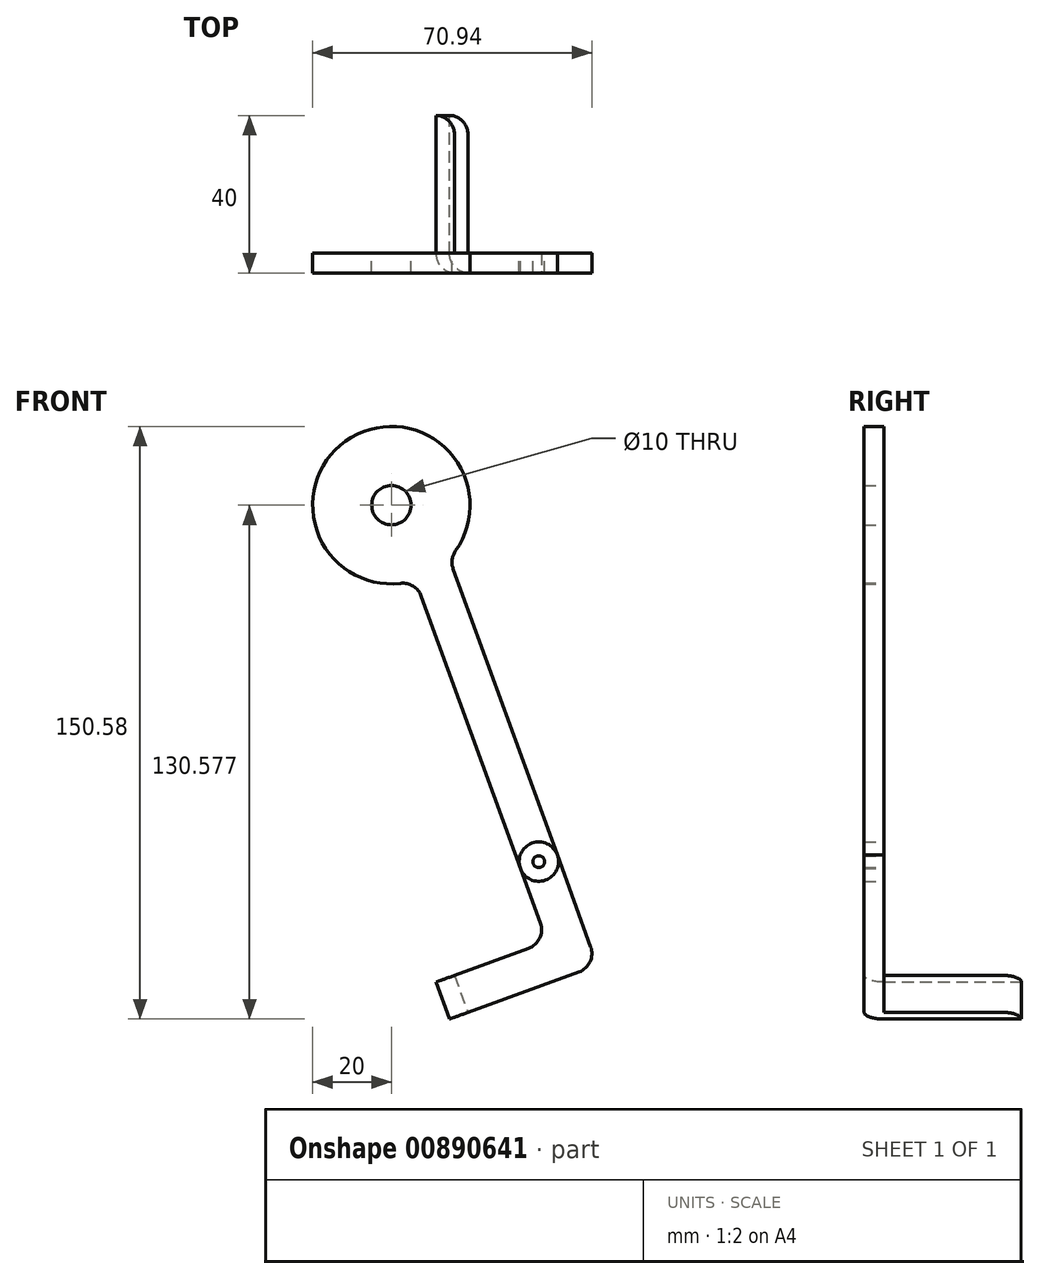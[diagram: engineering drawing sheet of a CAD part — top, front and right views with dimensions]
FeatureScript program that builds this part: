
annotation { "Feature Type Name" : "Feature", "Feature Type Description" : "" }
export const myFeature = defineFeature(function(context is Context, id is Id, definition is map)
    precondition{}
    {
        {
            var Q0;
            Q0=qCreatedBy(makeId("Front.planeOp"),FACE);
            var sketch = newSketch(context, id + "F0", { "sketchPlane" : qUnion([Q0])});
            skCircle(sketch, "E0", {"center": v(0, 33.82) * mm, "radius": 5 * mm});
            skLineSegment(sketch, "E1", {"start": v(0, 70.54) * mm, "end": v(0, -41.15) * mm, "construction": true});
            skCircle(sketch, "E2", {"center": v(0, 33.82) * mm, "radius": 20 * mm});
            skLineSegment(sketch, "E3.MirrorCS", {"start": v(36.77, -54.88) * mm, "end": v(32.07, -56.6) * mm, "construction": true});
            skLineSegment(sketch, "E4.MirrorCS", {"start": v(33.83, -60.2) * mm, "end": v(33.44, -60.35) * mm});
            skLineSegment(sketch, "E5.MirrorCS", {"start": v(32.46, -56.45) * mm, "end": v(32.07, -56.6) * mm});
            skLineSegment(sketch, "E6.MirrorCS", {"start": v(32.07, -56.6) * mm, "end": v(30.66, -57.1) * mm});
            skLineSegment(sketch, "E7.MirrorCS", {"start": v(30.66, -57.1) * mm, "end": v(32.03, -60.86) * mm});
            skLineSegment(sketch, "E8.MirrorCS", {"start": v(33.6, -60.82) * mm, "end": v(32.58, -58) * mm});
            skLineSegment(sketch, "E9.MirrorCS", {"start": v(37.45, -56.76) * mm, "end": v(38.14, -58.64) * mm, "construction": true});
            skLineSegment(sketch, "E10.MirrorCS", {"start": v(38.14, -58.64) * mm, "end": v(33.44, -60.35) * mm, "construction": true});
            skLineSegment(sketch, "E11.MirrorCS", {"start": v(37.45, -56.76) * mm, "end": v(36.77, -54.88) * mm, "construction": true});
            skCircle(sketch, "E12.MirrorC", {"center": v(37.45, -56.76) * mm, "radius": 1.5 * mm});
            skLineSegment(sketch, "E13.MirrorCS", {"start": v(30.66, -57.1) * mm, "end": v(25.92, -63.09) * mm});
            skLineSegment(sketch, "E14.MirrorCS", {"start": v(33.44, -60.35) * mm, "end": v(25.92, -63.09) * mm});
            skLineSegment(sketch, "E15.MirrorCS", {"start": v(24.55, -59.33) * mm, "end": v(25.92, -63.09) * mm});
            skLineSegment(sketch, "E16.MirrorCS", {"start": v(32.07, -56.6) * mm, "end": v(24.55, -59.33) * mm});
            skLineSegment(sketch, "E17.MirrorCS", {"start": v(6.1, 14.77) * mm, "end": v(32.58, -58) * mm});
            skLineSegment(sketch, "E18.MirrorCS", {"start": v(14.73, 20.29) * mm, "end": v(42.32, -55.52) * mm});
            skLineSegment(sketch, "E19.MirrorCS", {"start": v(16.04, -85.65) * mm, "end": v(19.46, -95.05) * mm});
            skLineSegment(sketch, "E20.MirrorCS", {"start": v(11.34, -87.36) * mm, "end": v(39.53, -77.1) * mm});
            skLineSegment(sketch, "E21.MirrorCS", {"start": v(14.76, -96.76) * mm, "end": v(11.34, -87.36) * mm});
            skLineSegment(sketch, "E22.MirrorCS", {"start": v(42.95, -86.5) * mm, "end": v(14.76, -96.76) * mm});
            skLineSegment(sketch, "E23.MirrorCS", {"start": v(52.35, -83.08) * mm, "end": v(42.95, -86.5) * mm});
            skLineSegment(sketch, "E24.MirrorCS", {"start": v(6.1, 14.77) * mm, "end": v(42.95, -86.5) * mm});
            skLineSegment(sketch, "E25.MirrorCS", {"start": v(14.73, 20.29) * mm, "end": v(52.35, -83.08) * mm});
            skCircle(sketch, "E26.MirrorC", {"center": v(37.45, -56.76) * mm, "radius": 5 * mm});
            skSolve(sketch);
        }
        {
            var Q0;
            Q0=makeQuery(id+"F0.imprint","IMPRINT",FACE,{"disambiguationData":[TD([[makeQuery(id+"F0.imprint","IMPRINT",EDGE,{"derivedFrom":sQuery(id+"F0.wireOp",EDGE,"E0")}),-1.0]])]});
            var Q1;
            {var subQ6=sQuery(id+"F0.wireOp",EDGE,"E5.MirrorCS");Q1=makeQuery(id+"F0.imprint","IMPRINT",FACE,{"disambiguationData":[TD([[makeQuery(id+"F0.imprint","IMPRINT",EDGE,{"derivedFrom":subQ6}),-1.0]])]});}
            var Q2;
            {var subQ0=sQuery(id+"F0.wireOp",EDGE,"E5.MirrorCS");Q2=makeQuery(id+"F0.imprint","IMPRINT",FACE,{"disambiguationData":[TD([[makeQuery(id+"F0.imprint","IMPRINT",EDGE,{"derivedFrom":subQ0}),1.0]])]});}
            var Q3;
            {var subQ0=sQuery(id+"F0.wireOp",EDGE,"E4.MirrorCS");Q3=makeQuery(id+"F0.imprint","IMPRINT",FACE,{"disambiguationData":[TD([[makeQuery(id+"F0.imprint","IMPRINT",EDGE,{"derivedFrom":subQ0}),-1.0]])]});}
            var Q4;
            Q4=makeQuery(id+"F0.imprint","IMPRINT",FACE,{"disambiguationData":[TD([[makeQuery(id+"F0.imprint","IMPRINT",EDGE,{"derivedFrom":sQuery(id+"F0.wireOp",EDGE,"E12.MirrorC")}),1.0]])]});
            var Q5;
            {var subQ3=sQuery(id+"F0.wireOp",EDGE,"E4.MirrorCS");Q5=makeQuery(id+"F0.imprint","IMPRINT",FACE,{"disambiguationData":[TD([[makeQuery(id+"F0.imprint","IMPRINT",EDGE,{"derivedFrom":subQ3}),1.0]])]});}
            var Q6;
            {var subQ0=sQuery(id+"F0.wireOp",EDGE,"E19.MirrorCS");Q6=makeQuery(id+"F0.imprint","IMPRINT",FACE,{"disambiguationData":[TD([[makeQuery(id+"F0.imprint","IMPRINT",EDGE,{"derivedFrom":subQ0}),1.0]])]});}
            var Q7;
            {var subQ0=sQuery(id+"F0.wireOp",EDGE,"E19.MirrorCS");Q7=makeQuery(id+"F0.imprint","IMPRINT",FACE,{"disambiguationData":[TD([[makeQuery(id+"F0.imprint","IMPRINT",EDGE,{"derivedFrom":subQ0}),-1.0]])]});}
            extrude(context, id + "F1", {"entities" : qUnion([Q0, Q1, Q2, Q3, Q4, Q5, Q6, Q7]), "depth" : 5 * mm, "offsetDistance" : 25 * mm});
        }
        {
            var Q0;
            {var subQ0=sQuery(id+"F0.wireOp",EDGE,"E19.MirrorCS");Q0=makeQuery(id+"F0.imprint","IMPRINT",FACE,{"disambiguationData":[TD([[makeQuery(id+"F0.imprint","IMPRINT",EDGE,{"derivedFrom":subQ0}),-1.0]])]});}
            extrude(context, id + "F2", {"entities" : qUnion([Q0]), "operationType" : NewBodyOperationType.ADD, "oppositeDirection" : true, "depth" : 35 * mm, "offsetDistance" : 25 * mm});
        }
        {
            var Q0;
            Q0=makeQuery(id+"F1.opExtrude","SWEPT_EDGE",EDGE,{"disambiguationData":[OSD([sQuery(id+"F0.wireOp",EDGE,"E2"),sQuery(id+"F0.wireOp",EDGE,"E24.MirrorCS")])]});
            var Q1;
            Q1=makeQuery(id+"F1.opExtrude","SWEPT_EDGE",EDGE,{"disambiguationData":[OSD([sQuery(id+"F0.wireOp",EDGE,"E2"),sQuery(id+"F0.wireOp",EDGE,"E18.MirrorCS")])]});
            var Q2;
            Q2=makeQuery(id+"F1.opExtrude","SWEPT_EDGE",EDGE,{"disambiguationData":[OSD([sQuery(id+"F0.wireOp",EDGE,"E23.MirrorCS"),sQuery(id+"F0.wireOp",EDGE,"E25.MirrorCS")])]});
            var Q3;
            Q3=makeQuery(id+"F2.opExtrude","CAP_EDGE",EDGE,{"disambiguationData":[OSD([sQuery(id+"F0.wireOp",EDGE,"E19.MirrorCS")])],"isStart":true});
            var Q4;
            Q4=makeQuery(id+"F1.opExtrude","CAP_EDGE",EDGE,{"disambiguationData":[OSD([sQuery(id+"F0.wireOp",EDGE,"E21.MirrorCS")])],"isStart":false});
            var Q5;
            Q5=makeQuery(id+"F1.opExtrude","SWEPT_EDGE",EDGE,{"disambiguationData":[OSD([sQuery(id+"F0.wireOp",EDGE,"E20.MirrorCS"),sQuery(id+"F0.wireOp",EDGE,"E24.MirrorCS")])]});
            var Q6;
            Q6=makeQuery(id+"F2.opExtrude","CAP_EDGE",EDGE,{"disambiguationData":[OSD([sQuery(id+"F0.wireOp",EDGE,"E19.MirrorCS")])],"isStart":false});
            fillet(context, id + "F3", {"entities" : qUnion([Q0, Q1, Q2, Q3, Q4, Q5, Q6]), "radius" : 5 * mm, "tangentPropagation" : true, "allowEdgeOverflow" : false});
        }
    });
